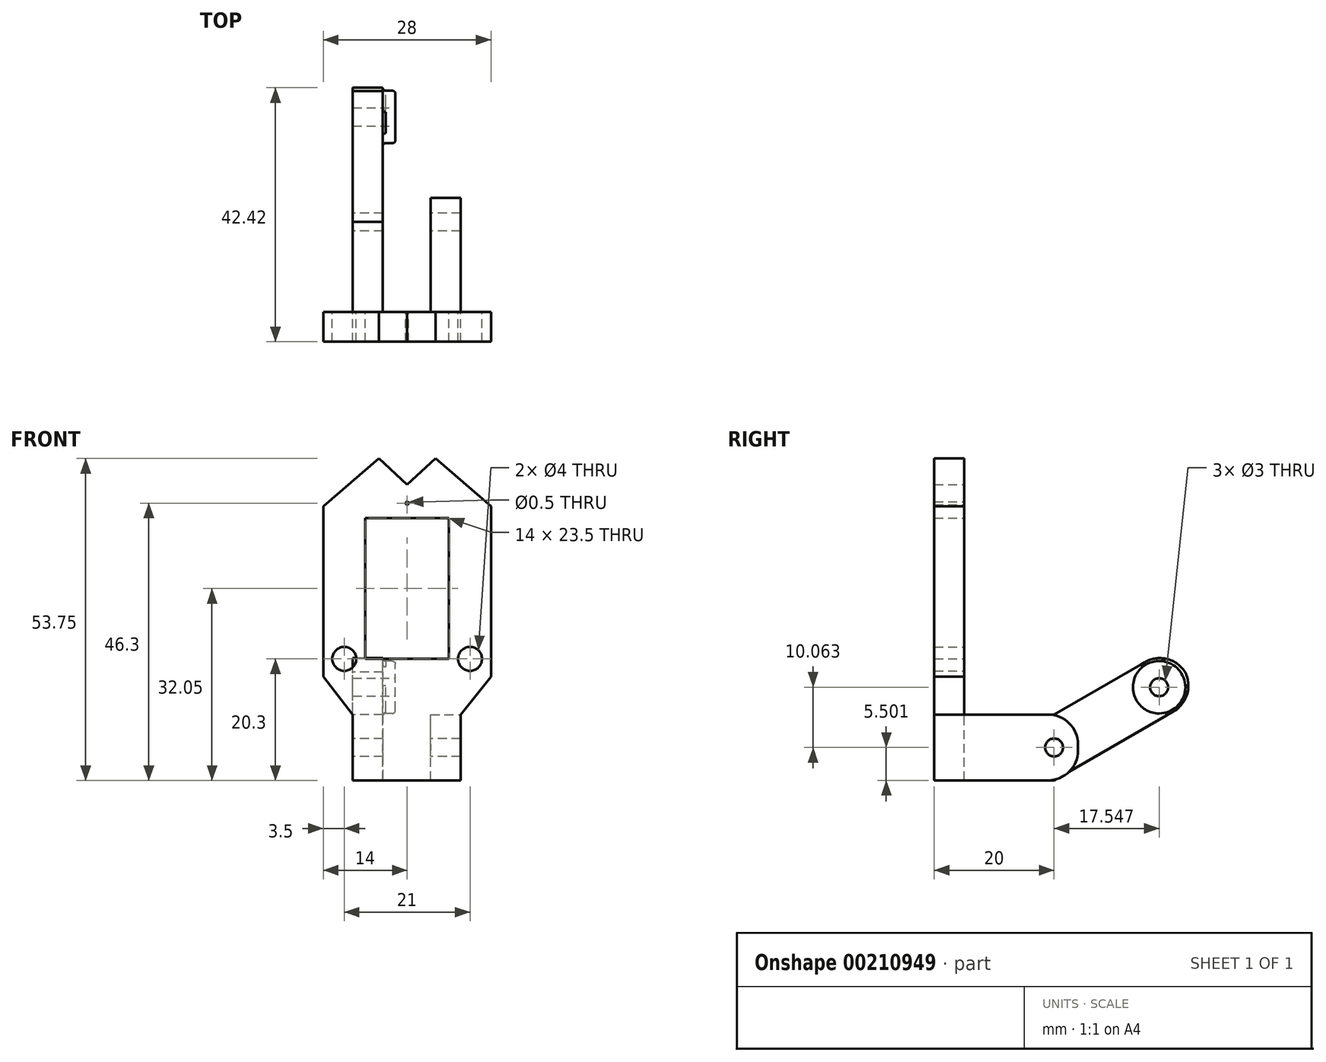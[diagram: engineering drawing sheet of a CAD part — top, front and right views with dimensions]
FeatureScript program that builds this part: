
annotation { "Feature Type Name" : "Feature", "Feature Type Description" : "" }
export const myFeature = defineFeature(function(context is Context, id is Id, definition is map)
    precondition{}
    {
        {
            var Q0;
            Q0=qCreatedBy(makeId("Front.planeOp"),FACE);
            var sketch = newSketch(context, id + "F0", { "sketchPlane" : qUnion([Q0])});
            skLineSegment(sketch, "E0.bottom", {"start": v(7, 11.75) * mm, "end": v(-7, 11.75) * mm});
            skLineSegment(sketch, "E0.top", {"start": v(7, -11.75) * mm, "end": v(-7, -11.75) * mm});
            skLineSegment(sketch, "E0.left", {"start": v(7, 11.75) * mm, "end": v(7, -11.75) * mm});
            skLineSegment(sketch, "E0.right", {"start": v(-7, 11.75) * mm, "end": v(-7, -11.75) * mm});
            skPoint(sketch, "E0.middle", {"position": v(0, 0) * mm});
            skLineSegment(sketch, "E1", {"start": v(7, 11.75) * mm, "end": v(14, 11.75) * mm});
            skLineSegment(sketch, "E2", {"start": v(-7, 11.75) * mm, "end": v(-14, 11.75) * mm});
            skLineSegment(sketch, "E3", {"start": v(14, 11.75) * mm, "end": v(14, -14.75) * mm});
            skLineSegment(sketch, "E4", {"start": v(-14, 11.75) * mm, "end": v(-14, -14.75) * mm});
            skLineSegment(sketch, "E5", {"start": v(-14, -14.75) * mm, "end": v(-9.07, -21.05) * mm});
            skLineSegment(sketch, "E6", {"start": v(-9.07, -21.05) * mm, "end": v(-9.07, -32.05) * mm});
            skPoint(sketch, "E7.end.orphan", {"position": v(0, 13.35) * mm});
            skLineSegment(sketch, "E8", {"start": v(-14, 11.75) * mm, "end": v(-14, 13.75) * mm});
            skLineSegment(sketch, "E9", {"start": v(14, 11.75) * mm, "end": v(14, 13.75) * mm});
            skLineSegment(sketch, "E10", {"start": v(-7, 11.75) * mm, "end": v(-7, 19.75) * mm});
            skLineSegment(sketch, "E11", {"start": v(7, 11.75) * mm, "end": v(7, 19.75) * mm});
            skLineSegment(sketch, "E12", {"start": v(-14, 13.75) * mm, "end": v(-7, 19.75) * mm});
            skLineSegment(sketch, "E13", {"start": v(14, 13.75) * mm, "end": v(7, 19.75) * mm});
            skPoint(sketch, "E14.start.orphan", {"position": v(0, 11.75) * mm});
            skLineSegment(sketch, "E15", {"start": v(0, 11.75) * mm, "end": v(0, 17.37) * mm});
            skLineSegment(sketch, "E16", {"start": v(-7, 19.75) * mm, "end": v(-4.72, 21.7) * mm});
            skLineSegment(sketch, "E17", {"start": v(-4.72, 21.7) * mm, "end": v(0, 17.37) * mm});
            skLineSegment(sketch, "E18", {"start": v(7, 19.75) * mm, "end": v(4.72, 21.7) * mm});
            skLineSegment(sketch, "E19", {"start": v(0, 17.37) * mm, "end": v(4.72, 21.7) * mm});
            skLineSegment(sketch, "E20", {"start": v(-9.07, -32.05) * mm, "end": v(8.93, -32.05) * mm});
            skLineSegment(sketch, "E21", {"start": v(8.93, -32.05) * mm, "end": v(8.93, -21.05) * mm});
            skLineSegment(sketch, "E22", {"start": v(8.93, -21.05) * mm, "end": v(14, -14.75) * mm});
            skLineSegment(sketch, "E23", {"start": v(7, -11.75) * mm, "end": v(10.5, -11.75) * mm});
            skLineSegment(sketch, "E24", {"start": v(-7, -11.75) * mm, "end": v(-10.5, -11.75) * mm});
            skLineSegment(sketch, "E25", {"start": v(0, 11.75) * mm, "end": v(0, 14.95) * mm});
            skLineSegment(sketch, "E26", {"start": v(0, 11.75) * mm, "end": v(0, 14.25) * mm});
            skPoint(sketch, "E27", {"position": v(0, 14.25) * mm});
            skSolve(sketch);
        }
        {
            var Q0;
            Q0=qCreatedBy(makeId("Top.planeOp"),FACE);
            var sketch = newSketch(context, id + "F1", { "sketchPlane" : qUnion([Q0])});
            skSolve(sketch);
        }
        {
            var Q0;
            Q0 = qSketchRegion(id + "F1", true);
            var Q1;
            Q1=makeQuery(id+"F0.imprint","IMPRINT",FACE,{"disambiguationData":[TD([[makeQuery(id+"F0.imprint","IMPRINT",EDGE,{"derivedFrom":sQuery(id+"F0.wireOp",EDGE,"E0.top")}),1.0]])]});
            var Q2;
            Q2=makeQuery(id+"F0.imprint","IMPRINT",FACE,{"disambiguationData":[TD([[makeQuery(id+"F0.imprint","IMPRINT",EDGE,{"derivedFrom":sQuery(id+"F0.wireOp",EDGE,"E2")}),-1.0]])]});
            var Q3;
            {var subQ0=sQuery(id+"F0.wireOp",EDGE,"E10");Q3=makeQuery(id+"F0.imprint","IMPRINT",FACE,{"disambiguationData":[TD([[makeQuery(id+"F0.imprint","IMPRINT",EDGE,{"derivedFrom":subQ0}),-1.0]])]});}
            var Q4;
            {var subQ0=sQuery(id+"F0.wireOp",EDGE,"E11");Q4=makeQuery(id+"F0.imprint","IMPRINT",FACE,{"disambiguationData":[TD([[makeQuery(id+"F0.imprint","IMPRINT",EDGE,{"derivedFrom":subQ0}),1.0]])]});}
            var Q5;
            Q5=makeQuery(id+"F0.imprint","IMPRINT",FACE,{"disambiguationData":[TD([[makeQuery(id+"F0.imprint","IMPRINT",EDGE,{"derivedFrom":sQuery(id+"F0.wireOp",EDGE,"E1")}),1.0]])]});
            extrude(context, id + "F2", {"entities" : qUnion([Q0, Q1, Q2, Q3, Q4, Q5]), "depth" : 5 * mm});
        }
        {
            var Q0;
            Q0=sQuery(id+"F0.wireOp",VERTEX,"E23.end");
            var Q1;
            Q1=makeQuery(id+"F2.opExtrude","SWEPT_BODY",BODY,{"disambiguationData":[OSD([sQuery(id+"F0.wireOp",EDGE,"E0.bottom"),sQuery(id+"F0.wireOp",EDGE,"E0.top"),sQuery(id+"F0.wireOp",EDGE,"E0.left"),sQuery(id+"F0.wireOp",EDGE,"E0.right"),sQuery(id+"F0.wireOp",EDGE,"E3"),sQuery(id+"F0.wireOp",EDGE,"E4"),sQuery(id+"F0.wireOp",EDGE,"E5"),sQuery(id+"F0.wireOp",EDGE,"E6"),sQuery(id+"F0.wireOp",EDGE,"E8"),sQuery(id+"F0.wireOp",EDGE,"E9"),sQuery(id+"F0.wireOp",EDGE,"E12"),sQuery(id+"F0.wireOp",EDGE,"E13"),sQuery(id+"F0.wireOp",EDGE,"E16"),sQuery(id+"F0.wireOp",EDGE,"E17"),sQuery(id+"F0.wireOp",EDGE,"E18"),sQuery(id+"F0.wireOp",EDGE,"E19"),sQuery(id+"F0.wireOp",EDGE,"E20"),sQuery(id+"F0.wireOp",EDGE,"E21"),sQuery(id+"F0.wireOp",EDGE,"E22")])]});
            hole(context, id + "F3", {"style" : HoleStyle.C_SINK, "endStyle" : HoleEndStyle.THROUGH, "oppositeDirection" : true, "holeDiameter" : 4 * mm, "cSinkDiameter" : 4 * mm, "cSinkAngle" : 90 * degree, "locations" : qUnion([Q0]), "scope" : qUnion([Q1]), "isTappedThrough" : true});
        }
        {
            var Q0;
            Q0=sQuery(id+"F0.wireOp",VERTEX,"E24.end");
            var Q1;
            Q1=makeQuery(id+"F2.opExtrude","SWEPT_BODY",BODY,{"disambiguationData":[OSD([sQuery(id+"F0.wireOp",EDGE,"E0.bottom"),sQuery(id+"F0.wireOp",EDGE,"E0.top"),sQuery(id+"F0.wireOp",EDGE,"E0.left"),sQuery(id+"F0.wireOp",EDGE,"E0.right"),sQuery(id+"F0.wireOp",EDGE,"E3"),sQuery(id+"F0.wireOp",EDGE,"E4"),sQuery(id+"F0.wireOp",EDGE,"E5"),sQuery(id+"F0.wireOp",EDGE,"E6"),sQuery(id+"F0.wireOp",EDGE,"E8"),sQuery(id+"F0.wireOp",EDGE,"E9"),sQuery(id+"F0.wireOp",EDGE,"E12"),sQuery(id+"F0.wireOp",EDGE,"E13"),sQuery(id+"F0.wireOp",EDGE,"E16"),sQuery(id+"F0.wireOp",EDGE,"E17"),sQuery(id+"F0.wireOp",EDGE,"E18"),sQuery(id+"F0.wireOp",EDGE,"E19"),sQuery(id+"F0.wireOp",EDGE,"E20"),sQuery(id+"F0.wireOp",EDGE,"E21"),sQuery(id+"F0.wireOp",EDGE,"E22")])]});
            hole(context, id + "F4", {"style" : HoleStyle.C_SINK, "endStyle" : HoleEndStyle.THROUGH, "oppositeDirection" : true, "holeDiameter" : 4 * mm, "cSinkDiameter" : 4 * mm, "cSinkAngle" : 90 * degree, "locations" : qUnion([Q0]), "scope" : qUnion([Q1]), "isTappedThrough" : true});
        }
        {
            var Q0;
            Q0=sQuery(id+"F0.wireOp",VERTEX,"E27");
            var Q1;
            Q1=makeQuery(id+"F2.opExtrude","SWEPT_BODY",BODY,{"disambiguationData":[OSD([sQuery(id+"F0.wireOp",EDGE,"E0.bottom"),sQuery(id+"F0.wireOp",EDGE,"E0.top"),sQuery(id+"F0.wireOp",EDGE,"E0.left"),sQuery(id+"F0.wireOp",EDGE,"E0.right"),sQuery(id+"F0.wireOp",EDGE,"E3"),sQuery(id+"F0.wireOp",EDGE,"E4"),sQuery(id+"F0.wireOp",EDGE,"E5"),sQuery(id+"F0.wireOp",EDGE,"E6"),sQuery(id+"F0.wireOp",EDGE,"E8"),sQuery(id+"F0.wireOp",EDGE,"E9"),sQuery(id+"F0.wireOp",EDGE,"E12"),sQuery(id+"F0.wireOp",EDGE,"E13"),sQuery(id+"F0.wireOp",EDGE,"E16"),sQuery(id+"F0.wireOp",EDGE,"E17"),sQuery(id+"F0.wireOp",EDGE,"E18"),sQuery(id+"F0.wireOp",EDGE,"E19"),sQuery(id+"F0.wireOp",EDGE,"E20"),sQuery(id+"F0.wireOp",EDGE,"E21"),sQuery(id+"F0.wireOp",EDGE,"E22")])]});
            hole(context, id + "F5", {"style" : HoleStyle.C_SINK, "endStyle" : HoleEndStyle.THROUGH, "oppositeDirection" : true, "holeDiameter" : 0.5 * mm, "cSinkDiameter" : 0.5 * mm, "cSinkAngle" : 90 * degree, "locations" : qUnion([Q0]), "scope" : qUnion([Q1]), "isTappedThrough" : true});
        }
        {
            var Q0;
            Q0=makeQuery(id+"F2.opExtrude","SWEPT_FACE",FACE,{"disambiguationData":[OSD([sQuery(id+"F0.wireOp",EDGE,"E6")])]});
            var sketch = newSketch(context, id + "F6", { "sketchPlane" : qUnion([Q0])});
            skLineSegment(sketch, "E28", {"start": v(0, -32.05) * mm, "end": v(-15, -32.05) * mm});
            skLineSegment(sketch, "E29", {"start": v(-15, -32.05) * mm, "end": v(-15, -21.05) * mm});
            skLineSegment(sketch, "E30", {"start": v(-15, -21.05) * mm, "end": v(0, -21.05) * mm});
            skLineSegment(sketch, "E31", {"start": v(-15, -32.05) * mm, "end": v(-39.25, -18.05) * mm});
            skLineSegment(sketch, "E32", {"start": v(-15, -21.05) * mm, "end": v(-34.49, -9.8) * mm});
            skLineSegment(sketch, "E33", {"start": v(-34.49, -9.8) * mm, "end": v(-39.25, -18.05) * mm});
            skSolve(sketch);
        }
        {
            var Q0;
            Q0 = qSketchRegion(id + "F6", true);
            var Q1;
            {var subQ0=sQuery(id+"F6.wireOp",EDGE,"E28");Q1=makeQuery(id+"F6.imprint","IMPRINT",FACE,{"disambiguationData":[TD([[makeQuery(id+"F6.imprint","IMPRINT",EDGE,{"derivedFrom":subQ0}),-1.0]])]});}
            extrude(context, id + "F7", {"entities" : qUnion([Q0, Q1]), "operationType" : NewBodyOperationType.ADD, "oppositeDirection" : true, "depth" : 5 * mm});
        }
        {
            var Q0;
            Q0=makeQuery(id+"F7.opExtrude","SWEPT_EDGE",EDGE,{"disambiguationData":[OSD([sQuery(id+"F6.wireOp",EDGE,"E32"),sQuery(id+"F6.wireOp",EDGE,"E33")])]});
            var Q1;
            Q1=makeQuery(id+"F7.opExtrude","SWEPT_EDGE",EDGE,{"disambiguationData":[OSD([sQuery(id+"F6.wireOp",EDGE,"E31"),sQuery(id+"F6.wireOp",EDGE,"E33")])]});
            fillet(context, id + "F8", {"entities" : qUnion([Q0, Q1]), "radius" : 5 * mm, "tangentPropagation" : true, "allowEdgeOverflow" : false});
        }
        {
            var Q0;
            Q0=makeQuery(id+"F7.opExtrude","CAP_FACE",FACE,{"disambiguationData":[OSD([sQuery(id+"F0.wireOp",EDGE,"E6"),sQuery(id+"F6.wireOp",EDGE,"E28"),sQuery(id+"F6.wireOp",EDGE,"E30"),sQuery(id+"F6.wireOp",EDGE,"E31"),sQuery(id+"F6.wireOp",EDGE,"E32"),sQuery(id+"F6.wireOp",EDGE,"E33")])],"isStart":false});
            var sketch = newSketch(context, id + "F9", { "sketchPlane" : qUnion([Q0])});
            skSolve(sketch);
        }
        {
            var Q0;
            {var subQ4=sQuery(id+"F6.wireOp",EDGE,"E28");Q0=makeQuery(id+"F9.imprint","IMPRINT",FACE,{"disambiguationData":[TD([[makeQuery(id+"F9.imprint","IMPRINT",EDGE,{"derivedFrom":makeQuery(id+"F7.opExtrude","CAP_EDGE",EDGE,{"disambiguationData":[OSD([subQ4])],"isStart":false})}),1.0]])]});}
            var sketch = newSketch(context, id + "F10", { "sketchPlane" : qUnion([Q0])});
            skPoint(sketch, "E34", {"position": v(32.55, -16.49) * mm});
            skCircle(sketch, "E35", {"center": v(32.55, -16.49) * mm, "radius": 4.38 * mm});
            skSolve(sketch);
        }
        {
            var Q0;
            Q0=makeQuery(id+"F10.imprint","IMPRINT",FACE,{"disambiguationData":[TD([[makeQuery(id+"F10.imprint","IMPRINT",EDGE,{"derivedFrom":sQuery(id+"F10.wireOp",EDGE,"E35")}),1.0]])]});
            extrude(context, id + "F11", {"entities" : qUnion([Q0]), "operationType" : NewBodyOperationType.ADD, "depth" : 2.1 * mm});
        }
        {
            var Q0;
            Q0=makeQuery(id+"F11.opExtrude","SWEPT_FACE",FACE,{"disambiguationData":[OSD([sQuery(id+"F10.wireOp",EDGE,"E35")])]});
            fillet(context, id + "F12", {"entities" : qUnion([Q0]), "radius" : 0.5 * mm, "tangentPropagation" : true, "allowEdgeOverflow" : false});
        }
        {
            var Q0;
            Q0=makeQuery(id+"F2.opExtrude","SWEPT_FACE",FACE,{"disambiguationData":[OSD([sQuery(id+"F0.wireOp",EDGE,"E21")])]});
            var sketch = newSketch(context, id + "F13", { "sketchPlane" : qUnion([Q0])});
            skLineSegment(sketch, "E36", {"start": v(0, -32.05) * mm, "end": v(19, -32.05) * mm});
            skLineSegment(sketch, "E37", {"start": v(0, -21.05) * mm, "end": v(19, -21.05) * mm});
            skLineSegment(sketch, "E38", {"start": v(19, -21.05) * mm, "end": v(19, -32.05) * mm});
            skSolve(sketch);
        }
        {
            var Q0;
            Q0=makeQuery(id+"F13.imprint","IMPRINT",FACE,{"disambiguationData":[TD([[makeQuery(id+"F13.imprint","IMPRINT",EDGE,{"derivedFrom":sQuery(id+"F13.wireOp",EDGE,"E36")}),1.0]])]});
            extrude(context, id + "F14", {"entities" : qUnion([Q0]), "operationType" : NewBodyOperationType.ADD, "oppositeDirection" : true, "depth" : 5 * mm});
        }
        {
            var Q0;
            Q0=makeQuery(id+"F14.opExtrude","SWEPT_EDGE",EDGE,{"disambiguationData":[OSD([sQuery(id+"F13.wireOp",EDGE,"E36"),sQuery(id+"F13.wireOp",EDGE,"E38")])]});
            var Q1;
            Q1=makeQuery(id+"F14.opExtrude","SWEPT_EDGE",EDGE,{"disambiguationData":[OSD([sQuery(id+"F13.wireOp",EDGE,"E37"),sQuery(id+"F13.wireOp",EDGE,"E38")])]});
            fillet(context, id + "F15", {"entities" : qUnion([Q0, Q1]), "radius" : 5 * mm, "tangentPropagation" : true, "allowEdgeOverflow" : false});
        }
        {
            var Q0;
            Q0=makeQuery(id+"F11.opExtrude","CAP_FACE",FACE,{"disambiguationData":[OSD([sQuery(id+"F10.wireOp",EDGE,"E35")])],"isStart":false});
            var sketch = newSketch(context, id + "F16", { "sketchPlane" : qUnion([Q0])});
            skPoint(sketch, "E39", {"position": v(32.55, -16.49) * mm});
            skSolve(sketch);
        }
        {
            var Q0;
            Q0=sQuery(id+"F16.wireOp",VERTEX,"E39");
            var Q1;
            Q1=makeQuery(id+"F2.opExtrude","SWEPT_BODY",BODY,{"disambiguationData":[OSD([sQuery(id+"F0.wireOp",EDGE,"E0.bottom"),sQuery(id+"F0.wireOp",EDGE,"E0.top"),sQuery(id+"F0.wireOp",EDGE,"E0.left"),sQuery(id+"F0.wireOp",EDGE,"E0.right"),sQuery(id+"F0.wireOp",EDGE,"E3"),sQuery(id+"F0.wireOp",EDGE,"E4"),sQuery(id+"F0.wireOp",EDGE,"E5"),sQuery(id+"F0.wireOp",EDGE,"E6"),sQuery(id+"F0.wireOp",EDGE,"E8"),sQuery(id+"F0.wireOp",EDGE,"E9"),sQuery(id+"F0.wireOp",EDGE,"E12"),sQuery(id+"F0.wireOp",EDGE,"E13"),sQuery(id+"F0.wireOp",EDGE,"E16"),sQuery(id+"F0.wireOp",EDGE,"E17"),sQuery(id+"F0.wireOp",EDGE,"E18"),sQuery(id+"F0.wireOp",EDGE,"E19"),sQuery(id+"F0.wireOp",EDGE,"E20"),sQuery(id+"F0.wireOp",EDGE,"E21"),sQuery(id+"F0.wireOp",EDGE,"E22")])]});
            hole(context, id + "F17", {"style" : HoleStyle.C_SINK, "endStyle" : HoleEndStyle.THROUGH, "holeDiameter" : 3 * mm, "cSinkDiameter" : 3 * mm, "cSinkAngle" : 90 * degree, "locations" : qUnion([Q0]), "scope" : qUnion([Q1]), "isTappedThrough" : true});
        }
        {
            var Q0;
            {var subQ0=sQuery(id+"F0.wireOp",EDGE,"E6");Q0=makeQuery(id+"F7.boolean.opBoolean","MERGE",FACE,{"derivedFrom":[makeQuery(id+"F2.opExtrude","SWEPT_FACE",FACE,{"disambiguationData":[OSD([subQ0])]}),makeQuery(id+"F7.opExtrude","CAP_FACE",FACE,{"disambiguationData":[OSD([subQ0,sQuery(id+"F6.wireOp",EDGE,"E28"),sQuery(id+"F6.wireOp",EDGE,"E30"),sQuery(id+"F6.wireOp",EDGE,"E31"),sQuery(id+"F6.wireOp",EDGE,"E32"),sQuery(id+"F6.wireOp",EDGE,"E33")])],"isStart":true})]});}
            var sketch = newSketch(context, id + "F18", { "sketchPlane" : qUnion([Q0])});
            skLineSegment(sketch, "E40", {"start": v(-15, -21.05) * mm, "end": v(-15, -26.55) * mm});
            skPoint(sketch, "E41", {"position": v(-15, -26.55) * mm});
            skSolve(sketch);
        }
        {
            var Q0;
            Q0=sQuery(id+"F18.wireOp",VERTEX,"E41");
            var Q1;
            Q1=makeQuery(id+"F2.opExtrude","SWEPT_BODY",BODY,{"disambiguationData":[OSD([sQuery(id+"F0.wireOp",EDGE,"E0.bottom"),sQuery(id+"F0.wireOp",EDGE,"E0.top"),sQuery(id+"F0.wireOp",EDGE,"E0.left"),sQuery(id+"F0.wireOp",EDGE,"E0.right"),sQuery(id+"F0.wireOp",EDGE,"E3"),sQuery(id+"F0.wireOp",EDGE,"E4"),sQuery(id+"F0.wireOp",EDGE,"E5"),sQuery(id+"F0.wireOp",EDGE,"E6"),sQuery(id+"F0.wireOp",EDGE,"E8"),sQuery(id+"F0.wireOp",EDGE,"E9"),sQuery(id+"F0.wireOp",EDGE,"E12"),sQuery(id+"F0.wireOp",EDGE,"E13"),sQuery(id+"F0.wireOp",EDGE,"E16"),sQuery(id+"F0.wireOp",EDGE,"E17"),sQuery(id+"F0.wireOp",EDGE,"E18"),sQuery(id+"F0.wireOp",EDGE,"E19"),sQuery(id+"F0.wireOp",EDGE,"E20"),sQuery(id+"F0.wireOp",EDGE,"E21"),sQuery(id+"F0.wireOp",EDGE,"E22")])]});
            hole(context, id + "F19", {"style" : HoleStyle.C_SINK, "endStyle" : HoleEndStyle.THROUGH, "holeDiameter" : 3 * mm, "cSinkDiameter" : 3 * mm, "cSinkAngle" : 90 * degree, "locations" : qUnion([Q0]), "scope" : qUnion([Q1]), "isTappedThrough" : true});
        }
    });
